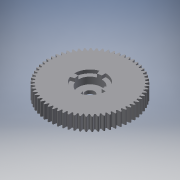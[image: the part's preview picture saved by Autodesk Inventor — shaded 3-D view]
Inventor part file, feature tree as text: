
AUTODESK INVENTOR PART (.ipt)
format: ipt  version: 2017 (Build 210142000, 142)  size: 386,048 bytes
history: native  units: mm
features: extrude x5, sketch x4, pattern_circular x2
ambient origin geometry x8: Origin, YZ Plane, XZ Plane, XY Plane, X Axis, Y Axis, Z Axis, Center Point
bodies: Solid1 (feature_tree)
feature tree (11):
  sketch  "Sketch1"  dims[d0=20.0mm d1=0.0mm]
  extrude  "Extrusion1"  TaperAngle=0.0deg  [1 undecoded]
  extrude  "Extrusion2"  Depth=10.0mm TaperAngle=360.0deg
  pattern_circular  "Circular Pattern1"  [2 undecoded]
  extrude  "Extrusion3"  Depth=15.0mm TaperAngle=0.0deg
  extrude  "Extrusion4"  Depth=5.0mm
  extrude  "Extrusion5"  Depth=5.0mm
  pattern_circular  "Circular Pattern2"  [2 undecoded]
  sketch  "Sketch2"  dims[d2=10.0mm d3=0.0mm d4=610.0mm d5=360.0deg]
  sketch  "Sketch3"  dims[d7=13.5mm]
  sketch  "Sketch4"  dims[d8=10.0mm d9=0.0mm d10=35.0mm d11=15.0mm d12=0.0mm d13=6.0mm d14=12.217305mm d15=5.0mm d16=0.0mm d17=40.0mm d18=360.0deg]
note: 5 required parameter values undecoded (feature->parameter linkage not recoverable at this tier; creation-order binding heuristic only, values carry confidence <= 0.55)
